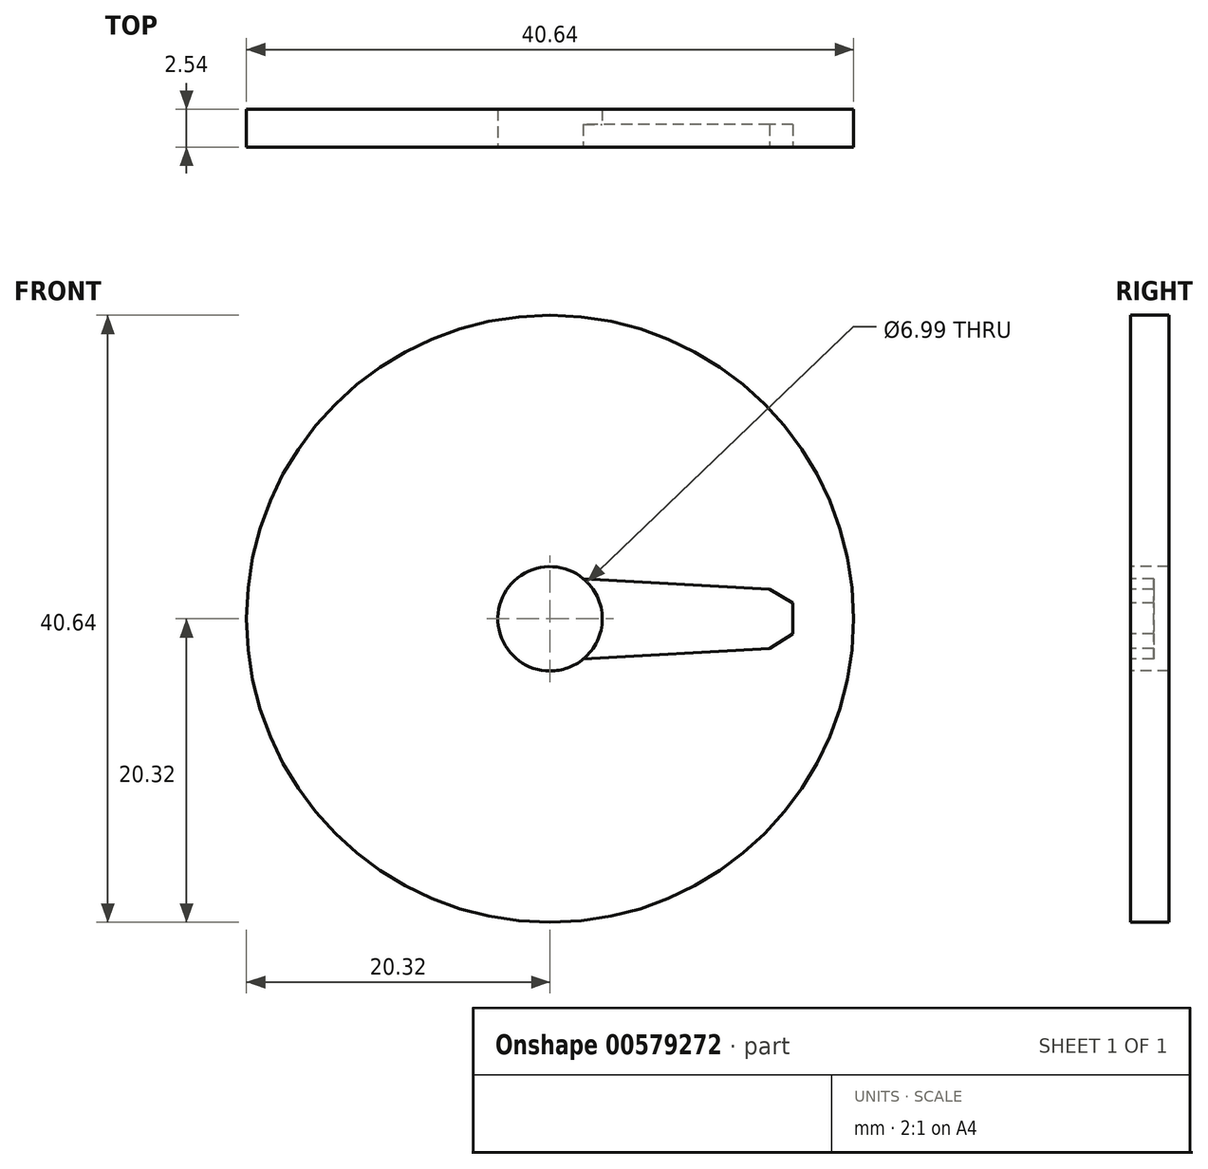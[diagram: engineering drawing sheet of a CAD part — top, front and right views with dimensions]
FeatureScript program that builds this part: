
annotation { "Feature Type Name" : "Feature", "Feature Type Description" : "" }
export const myFeature = defineFeature(function(context is Context, id is Id, definition is map)
    precondition{}
    {
        {
            var Q0;
            Q0=qCreatedBy(makeId("Front.planeOp"),FACE);
            var sketch = newSketch(context, id + "F0", { "sketchPlane" : qUnion([Q0])});
            skCircle(sketch, "E0", {"center": v(0, 0) * mm, "radius": 20.32 * mm});
            skSolve(sketch);
        }
        {
            var Q0;
            Q0=makeQuery(id+"F0.imprint","IMPRINT",FACE,{"disambiguationData":[TD([[makeQuery(id+"F0.imprint","IMPRINT",EDGE,{"derivedFrom":sQuery(id+"F0.wireOp",EDGE,"E0")}),1.0]])]});
            extrude(context, id + "F1", {"entities" : qUnion([Q0]), "depth" : 2.54 * mm, "offsetDistance" : 25.4 * mm});
        }
        {
            var Q0;
            Q0=makeQuery(id+"F1.opExtrude","CAP_FACE",FACE,{"disambiguationData":[OSD([sQuery(id+"F0.wireOp",EDGE,"E0")])],"isStart":false});
            var sketch = newSketch(context, id + "F2", { "sketchPlane" : qUnion([Q0])});
            skCircle(sketch, "E1", {"center": v(0, 0) * mm, "radius": 3.5 * mm});
            skSolve(sketch);
        }
        {
            var Q0;
            Q0=makeQuery(id+"F2.imprint","IMPRINT",FACE,{"disambiguationData":[TD([[makeQuery(id+"F2.imprint","IMPRINT",EDGE,{"derivedFrom":sQuery(id+"F2.wireOp",EDGE,"E1")}),1.0]])]});
            var Q1;
            Q1=sQuery(id+"F2.wireOp",EDGE,"E1");
            extrude(context, id + "F3", {"entities" : qUnion([Q0]), "operationType" : NewBodyOperationType.REMOVE, "surfaceEntities" : qUnion([Q1]), "oppositeDirection" : true, "depth" : 25.4 * mm, "offsetDistance" : 25.4 * mm});
        }
        {
            var Q0;
            Q0=makeQuery(id+"F1.opExtrude","CAP_FACE",FACE,{"disambiguationData":[OSD([sQuery(id+"F0.wireOp",EDGE,"E0")])],"isStart":false});
            var sketch = newSketch(context, id + "F4", { "sketchPlane" : qUnion([Q0])});
            skLineSegment(sketch, "E2.right", {"start": v(-31.75, 2.7) * mm, "end": v(-31.75, -2.7) * mm});
            skPoint(sketch, "E2.middle", {"position": v(0, 0) * mm});
            skLineSegment(sketch, "E3", {"start": v(2.22, 2.7) * mm, "end": v(14.7, 2) * mm});
            skLineSegment(sketch, "E4", {"start": v(14.7, 2) * mm, "end": v(16.26, 1.05) * mm});
            skLineSegment(sketch, "E5", {"start": v(16.26, -1) * mm, "end": v(14.7, -2) * mm});
            skLineSegment(sketch, "E6", {"start": v(14.7, -2) * mm, "end": v(2.22, -2.7) * mm});
            skPoint(sketch, "E6.endSnap0", {"position": v(0, -2.7) * mm});
            skLineSegment(sketch, "E7", {"start": v(2.22, -2.7) * mm, "end": v(2.22, 2.7) * mm});
            skLineSegment(sketch, "E8", {"start": v(16.26, 1.05) * mm, "end": v(16.26, -1) * mm});
            skSolve(sketch);
        }
        {
            var Q0;
            Q0 = qSketchRegion(id + "F4", true);
            extrude(context, id + "F5", {"entities" : qUnion([Q0]), "operationType" : NewBodyOperationType.REMOVE, "oppositeDirection" : true, "depth" : 1.52 * mm, "offsetDistance" : 25.4 * mm});
        }
    });
